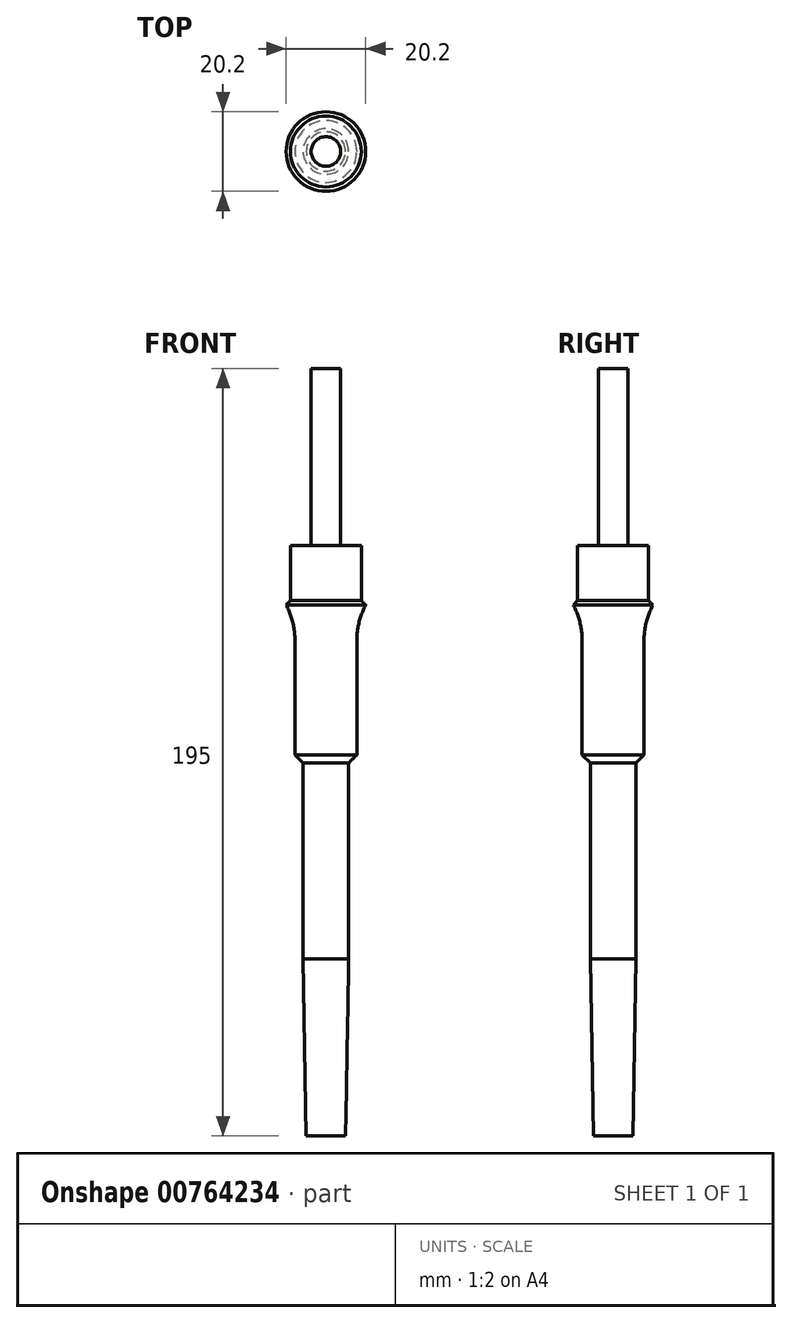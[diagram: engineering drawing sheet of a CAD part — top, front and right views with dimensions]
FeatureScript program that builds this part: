
annotation { "Feature Type Name" : "Feature", "Feature Type Description" : "" }
export const myFeature = defineFeature(function(context is Context, id is Id, definition is map)
    precondition{}
    {
        {
            var Q0;
            Q0=qCreatedBy(makeId("Front.planeOp"),FACE);
            var sketch = newSketch(context, id + "F0", { "sketchPlane" : qUnion([Q0])});
            skLineSegment(sketch, "E0", {"start": v(0, -150) * mm, "end": v(5, -150) * mm});
            skLineSegment(sketch, "E1", {"start": v(5, -150) * mm, "end": v(5.8, -105) * mm});
            skLineSegment(sketch, "E2", {"start": v(5.8, -105) * mm, "end": v(5.8, -55.26) * mm});
            skLineSegment(sketch, "E3", {"start": v(3.75, 45) * mm, "end": v(0, 45) * mm});
            skLineSegment(sketch, "E4", {"start": v(0, 45) * mm, "end": v(0, -150) * mm});
            skLineSegment(sketch, "E5", {"start": v(5.8, -55.26) * mm, "end": v(7.85, -53.2) * mm});
            skLineSegment(sketch, "E6", {"start": v(7.85, -53.2) * mm, "end": v(7.85, -24.32) * mm});
            skLineSegment(sketch, "E7", {"start": v(10.1, -15.1) * mm, "end": v(9, -14) * mm});
            skArc(sketch, "E8", {"start": v(10.1, -15.1) * mm, "mid": v(8.42, -19.57) * mm, "end": v(7.85, -24.32) * mm});
            skLineSegment(sketch, "E9", {"start": v(9, -14) * mm, "end": v(9, 0) * mm});
            skLineSegment(sketch, "E10", {"start": v(3.75, 0) * mm, "end": v(9, 0) * mm});
            skLineSegment(sketch, "E11", {"start": v(3.75, 0) * mm, "end": v(3.75, 45) * mm});
            skSolve(sketch);
        }
        {
            var Q0;
            Q0 = qSketchRegion(id + "F0", true);
            var Q1;
            Q1=sQuery(id+"F0.wireOp",EDGE,"E4");
            revolve(context, id + "F1", {"surfaceOperationType" : NewSurfaceOperationType.NEW, "entities" : qUnion([Q0]), "axis" : qUnion([Q1]), "revolveType" : RevolveType.FULL});
        }
    });
